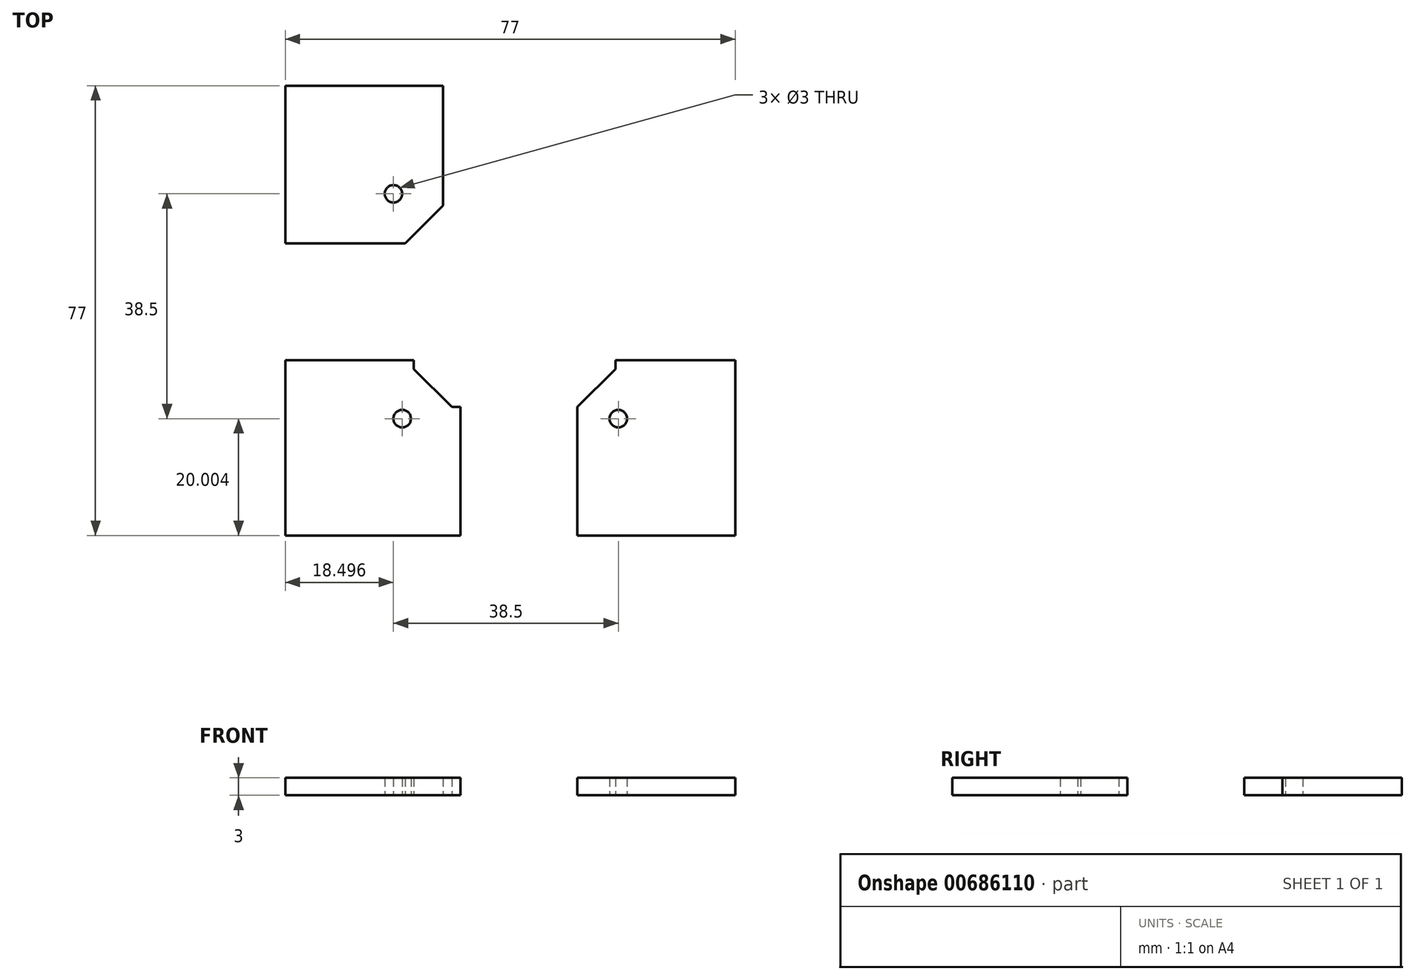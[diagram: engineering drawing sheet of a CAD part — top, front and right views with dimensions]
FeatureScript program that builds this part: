
annotation { "Feature Type Name" : "Feature", "Feature Type Description" : "" }
export const myFeature = defineFeature(function(context is Context, id is Id, definition is map)
    precondition{}
    {
        {
            var Q0;
            Q0=qCreatedBy(makeId("Top.planeOp"),FACE);
            var sketch = newSketch(context, id + "F0", { "sketchPlane" : qUnion([Q0])});
            skLineSegment(sketch, "E0.bottom", {"start": v(-24.9, 7.85) * mm, "end": v(5.1, 7.85) * mm});
            skLineSegment(sketch, "E0.top", {"start": v(-24.9, -22.15) * mm, "end": v(5.1, -22.15) * mm});
            skLineSegment(sketch, "E0.left", {"start": v(-24.9, 7.85) * mm, "end": v(-24.9, -22.15) * mm});
            skLineSegment(sketch, "E0.right", {"start": v(5.1, 7.85) * mm, "end": v(5.1, -22.15) * mm});
            skLineSegment(sketch, "E1", {"start": v(-2.9, 7.85) * mm, "end": v(-2.9, 6.35) * mm});
            skLineSegment(sketch, "E2", {"start": v(-2.9, 6.35) * mm, "end": v(3.6, -0.15) * mm});
            skLineSegment(sketch, "E3", {"start": v(3.6, -0.15) * mm, "end": v(5.1, -0.15) * mm});
            skLineSegment(sketch, "E4", {"start": v(-4.9, 7.85) * mm, "end": v(-4.9, -2.15) * mm, "construction": true});
            skCircle(sketch, "E5", {"center": v(-4.9, -2.15) * mm, "radius": 1.5 * mm});
            skLineSegment(sketch, "E6.bottom", {"start": v(-24.9, 54.85) * mm, "end": v(2.1, 54.85) * mm});
            skLineSegment(sketch, "E6.top", {"start": v(-24.9, 27.85) * mm, "end": v(2.1, 27.85) * mm});
            skLineSegment(sketch, "E6.left", {"start": v(-24.9, 54.85) * mm, "end": v(-24.9, 27.85) * mm});
            skLineSegment(sketch, "E6.right", {"start": v(2.1, 54.85) * mm, "end": v(2.1, 27.85) * mm});
            skLineSegment(sketch, "E7", {"start": v(-4.4, 27.85) * mm, "end": v(2.1, 34.35) * mm});
            skLineSegment(sketch, "E8.bottom", {"start": v(25.1, 7.85) * mm, "end": v(52.1, 7.85) * mm});
            skLineSegment(sketch, "E8.top", {"start": v(25.1, -22.15) * mm, "end": v(52.1, -22.15) * mm});
            skLineSegment(sketch, "E8.left", {"start": v(25.1, 7.85) * mm, "end": v(25.1, -22.15) * mm});
            skLineSegment(sketch, "E8.right", {"start": v(52.1, 7.85) * mm, "end": v(52.1, -22.15) * mm});
            skLineSegment(sketch, "E9", {"start": v(25.1, -0.15) * mm, "end": v(31.6, 6.35) * mm});
            skLineSegment(sketch, "E10", {"start": v(31.6, 6.35) * mm, "end": v(31.6, 7.85) * mm});
            skLineSegment(sketch, "E11", {"start": v(-24.9, 27.85) * mm, "end": v(-24.9, 7.85) * mm, "construction": true});
            skLineSegment(sketch, "E12", {"start": v(5.1, -22.15) * mm, "end": v(25.1, -22.15) * mm, "construction": true});
            skLineSegment(sketch, "E13", {"start": v(-6.4, 27.85) * mm, "end": v(-6.4, 36.35) * mm, "construction": true});
            skCircle(sketch, "E14", {"center": v(-6.4, 36.35) * mm, "radius": 1.5 * mm});
            skLineSegment(sketch, "E15", {"start": v(25.1, -2.15) * mm, "end": v(32.1, -2.15) * mm, "construction": true});
            skCircle(sketch, "E16", {"center": v(32.1, -2.15) * mm, "radius": 1.5 * mm});
            skSolve(sketch);
        }
        {
            var Q0;
            {var subQ1=sQuery(id+"F0.wireOp",EDGE,"E0.top");Q0=makeQuery(id+"F0.imprint","IMPRINT",FACE,{"disambiguationData":[TD([[makeQuery(id+"F0.imprint","IMPRINT",EDGE,{"derivedFrom":subQ1}),1.0]])]});}
            var Q1;
            {var subQ2=sQuery(id+"F0.wireOp",EDGE,"E8.top");Q1=makeQuery(id+"F0.imprint","IMPRINT",FACE,{"disambiguationData":[TD([[makeQuery(id+"F0.imprint","IMPRINT",EDGE,{"derivedFrom":subQ2}),1.0]])]});}
            var Q2;
            {var subQ1=sQuery(id+"F0.wireOp",EDGE,"E6.bottom");Q2=makeQuery(id+"F0.imprint","IMPRINT",FACE,{"disambiguationData":[TD([[makeQuery(id+"F0.imprint","IMPRINT",EDGE,{"derivedFrom":subQ1}),-1.0]])]});}
            extrude(context, id + "F1", {"entities" : qUnion([Q0, Q1, Q2]), "depth" : 3 * mm, "offsetDistance" : 25 * mm});
        }
    });
